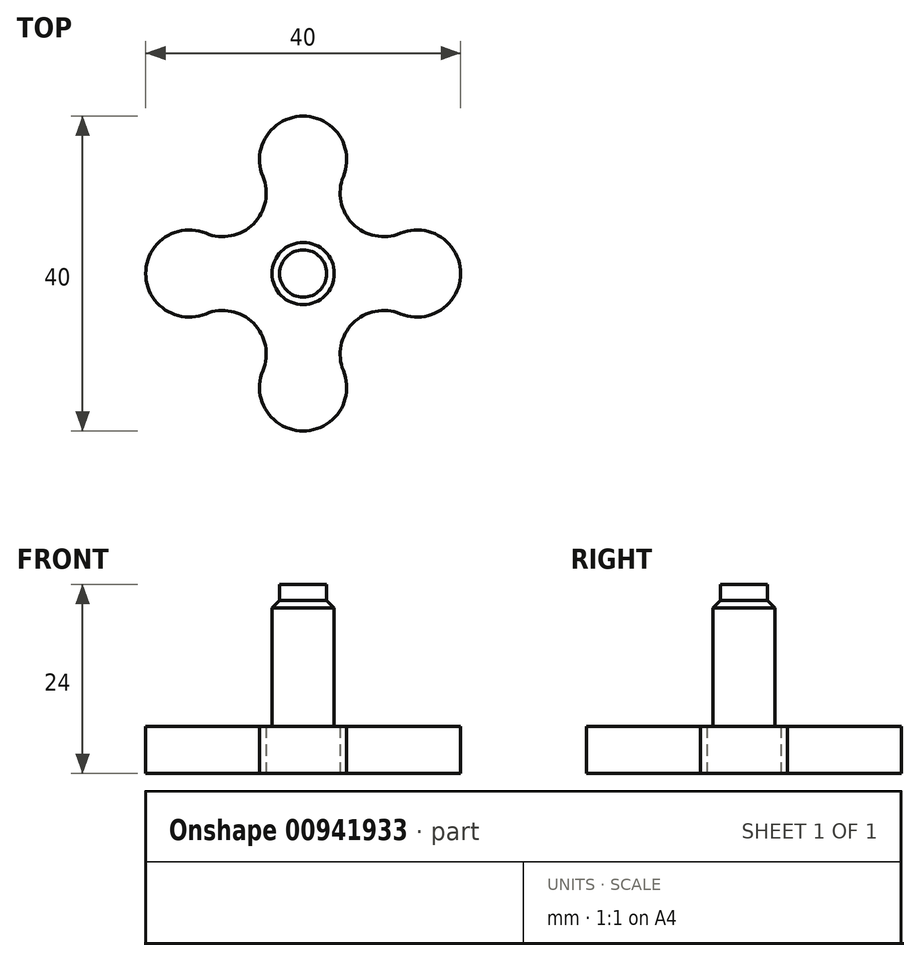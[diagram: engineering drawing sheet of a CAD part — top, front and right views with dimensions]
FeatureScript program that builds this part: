
annotation { "Feature Type Name" : "Feature", "Feature Type Description" : "" }
export const myFeature = defineFeature(function(context is Context, id is Id, definition is map)
    precondition{}
    {
        {
            var Q0;
            Q0=qCreatedBy(makeId("Front.planeOp"),FACE);
            var sketch = newSketch(context, id + "F0", { "sketchPlane" : qUnion([Q0])});
            skLineSegment(sketch, "E0", {"start": v(0, 24) * mm, "end": v(0, -11.74) * mm});
            skLineSegment(sketch, "E1", {"start": v(0, 24) * mm, "end": v(3, 24) * mm});
            skLineSegment(sketch, "E2", {"start": v(3, 24) * mm, "end": v(3, 21.95) * mm});
            skLineSegment(sketch, "E3", {"start": v(3, 21.95) * mm, "end": v(3.95, 21) * mm});
            skLineSegment(sketch, "E4", {"start": v(3.95, 21) * mm, "end": v(3.95, 6) * mm});
            skLineSegment(sketch, "E5", {"start": v(3.95, 6) * mm, "end": v(20, 6) * mm});
            skLineSegment(sketch, "E6", {"start": v(20, 6) * mm, "end": v(20, 0) * mm});
            skLineSegment(sketch, "E7", {"start": v(20, 0) * mm, "end": v(0, 0) * mm});
            skSolve(sketch);
        }
        {
            var Q0;
            {var subQ0=sQuery(id+"F0.wireOp",EDGE,"E1");Q0=makeQuery(id+"F0.imprint","IMPRINT",FACE,{"disambiguationData":[TD([[makeQuery(id+"F0.imprint","IMPRINT",EDGE,{"derivedFrom":subQ0}),-1.0]])]});}
            var Q1;
            Q1=sQuery(id+"F0.wireOp",EDGE,"E0");
            revolve(context, id + "F1", {"surfaceOperationType" : NewSurfaceOperationType.NEW, "entities" : qUnion([Q0]), "axis" : qUnion([Q1]), "revolveType" : RevolveType.FULL});
        }
        {
            var Q0;
            Q0=makeQuery(id+"F1.opRevolve","SWEPT_FACE",FACE,{"disambiguationData":[OSD([sQuery(id+"F0.wireOp",EDGE,"E7")])]});
            var sketch = newSketch(context, id + "F2", { "sketchPlane" : qUnion([Q0])});
            skCircle(sketch, "E8.0", {"center": v(0, 0) * mm, "radius": 20 * mm});
            skLineSegment(sketch, "E9", {"start": v(0, 26.26) * mm, "end": v(0, -23.96) * mm});
            skLineSegment(sketch, "E10", {"start": v(-27.96, 0) * mm, "end": v(26.78, 0) * mm});
            skArc(sketch, "E11", {"start": v(5.11, 12.35) * mm, "mid": v(0, 20) * mm, "end": v(-5.11, 12.35) * mm});
            skArc(sketch, "E12.1.0", {"start": v(-12.35, 5.11) * mm, "mid": v(-6.31, 6.31) * mm, "end": v(-5.11, 12.35) * mm});
            skArc(sketch, "E12.2.0", {"start": v(-12.35, 5.11) * mm, "mid": v(-20, 0) * mm, "end": v(-12.35, -5.11) * mm});
            skArc(sketch, "E12.3.0", {"start": v(-5.11, -12.35) * mm, "mid": v(-6.31, -6.31) * mm, "end": v(-12.35, -5.11) * mm});
            skArc(sketch, "E12.4.0", {"start": v(-5.11, -12.35) * mm, "mid": v(0, -20) * mm, "end": v(5.11, -12.35) * mm});
            skArc(sketch, "E12.5.0", {"start": v(12.35, -5.11) * mm, "mid": v(6.31, -6.31) * mm, "end": v(5.11, -12.35) * mm});
            skArc(sketch, "E12.6.0", {"start": v(12.35, -5.11) * mm, "mid": v(20, 0) * mm, "end": v(12.35, 5.11) * mm});
            skArc(sketch, "E12.7.0", {"start": v(5.11, 12.35) * mm, "mid": v(6.31, 6.31) * mm, "end": v(12.35, 5.11) * mm});
            skSolve(sketch);
        }
        {
            var Q0;
            {var subQ5=sQuery(id+"F2.wireOp",EDGE,"E12.5.0");Q0=makeQuery(id+"F2.imprint","IMPRINT",FACE,{"disambiguationData":[TD([[makeQuery(id+"F2.imprint","IMPRINT",EDGE,{"derivedFrom":subQ5}),1.0]])]});}
            var Q1;
            {var subQ5=sQuery(id+"F2.wireOp",EDGE,"E12.7.0");Q1=makeQuery(id+"F2.imprint","IMPRINT",FACE,{"disambiguationData":[TD([[makeQuery(id+"F2.imprint","IMPRINT",EDGE,{"derivedFrom":subQ5}),1.0]])]});}
            var Q2;
            {var subQ5=sQuery(id+"F2.wireOp",EDGE,"E12.1.0");Q2=makeQuery(id+"F2.imprint","IMPRINT",FACE,{"disambiguationData":[TD([[makeQuery(id+"F2.imprint","IMPRINT",EDGE,{"derivedFrom":subQ5}),1.0]])]});}
            var Q3;
            {var subQ5=sQuery(id+"F2.wireOp",EDGE,"E12.3.0");Q3=makeQuery(id+"F2.imprint","IMPRINT",FACE,{"disambiguationData":[TD([[makeQuery(id+"F2.imprint","IMPRINT",EDGE,{"derivedFrom":subQ5}),1.0]])]});}
            extrude(context, id + "F3", {"entities" : qUnion([Q0, Q1, Q2, Q3]), "operationType" : NewBodyOperationType.REMOVE, "endBound" : BoundingType.THROUGH_ALL, "oppositeDirection" : true, "depth" : 25 * mm, "offsetDistance" : 25 * mm});
        }
    });
